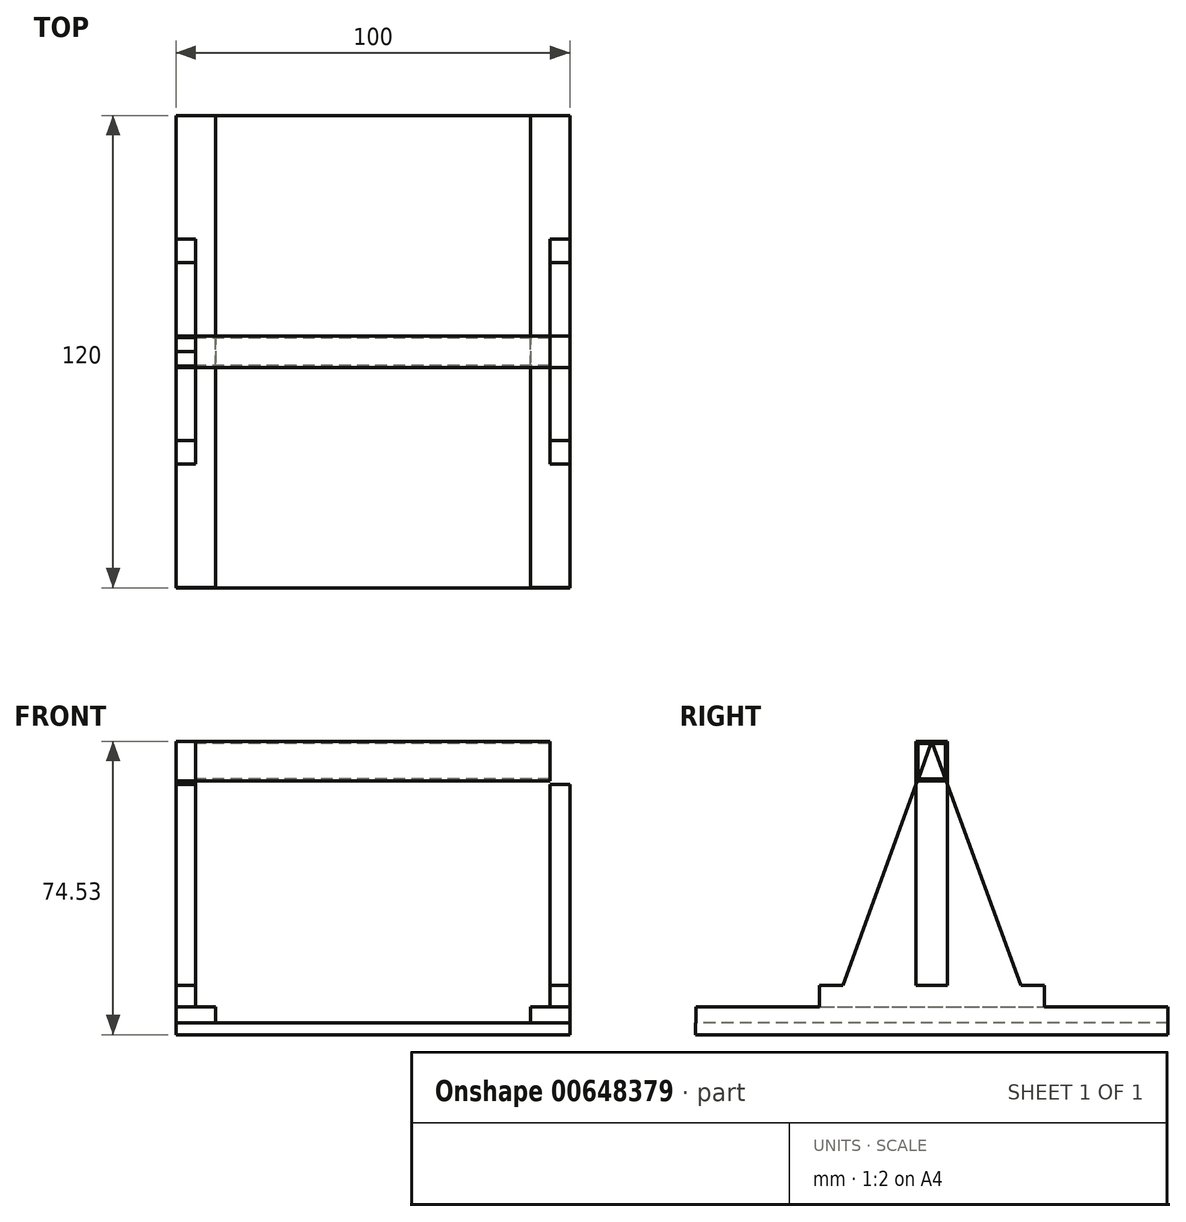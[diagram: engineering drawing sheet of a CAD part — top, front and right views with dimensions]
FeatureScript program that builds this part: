
annotation { "Feature Type Name" : "Feature", "Feature Type Description" : "" }
export const myFeature = defineFeature(function(context is Context, id is Id, definition is map)
    precondition{}
    {
        {
            var Q0;
            Q0=qCreatedBy(makeId("Right.planeOp"),FACE);
            cPlane(context, id + "F0", {"entities" : qUnion([Q0]), "cplaneType" : CPlaneType.OFFSET, "offset" : 50 * mm, "oppositeDirection" : true, "width" : 150 * mm, "height" : 150 * mm});
        }
        {
            var Q0;
            Q0=qCreatedBy(id+"F0.planeOp",FACE);
            var sketch = newSketch(context, id + "F1", { "sketchPlane" : qUnion([Q0])});
            skLineSegment(sketch, "E0", {"start": v(0, 0) * mm, "end": v(0, 62.03) * mm});
            skLineSegment(sketch, "E1", {"start": v(0, 0) * mm, "end": v(-22.58, 0) * mm});
            skLineSegment(sketch, "E2", {"start": v(-22.58, 0) * mm, "end": v(0, 62.03) * mm});
            skLineSegment(sketch, "E3.MirrorCS", {"start": v(22.58, 0) * mm, "end": v(0, 62.03) * mm});
            skLineSegment(sketch, "E4.MirrorCS", {"start": v(0, 0) * mm, "end": v(22.58, 0) * mm});
            skLineSegment(sketch, "E5.bottom", {"start": v(-28.58, 0) * mm, "end": v(28.58, 0) * mm});
            skLineSegment(sketch, "E5.top", {"start": v(-28.58, -5.5) * mm, "end": v(28.58, -5.5) * mm});
            skLineSegment(sketch, "E5.left", {"start": v(-28.58, 0) * mm, "end": v(-28.58, -5.5) * mm});
            skLineSegment(sketch, "E5.right", {"start": v(28.58, 0) * mm, "end": v(28.58, -5.5) * mm});
            skLineSegment(sketch, "E6.bottom", {"start": v(4, 0) * mm, "end": v(-4, 0) * mm});
            skLineSegment(sketch, "E6.top", {"start": v(4, 62.03) * mm, "end": v(-4, 62.03) * mm});
            skLineSegment(sketch, "E6.left", {"start": v(4, 0) * mm, "end": v(4, 62.03) * mm});
            skLineSegment(sketch, "E6.right", {"start": v(-4, 0) * mm, "end": v(-4, 62.03) * mm});
            skLineSegment(sketch, "E7.bottom", {"start": v(60, -0.5) * mm, "end": v(-59.95, -0.5) * mm});
            skLineSegment(sketch, "E7.top", {"start": v(60, -9.5) * mm, "end": v(-59.95, -9.5) * mm});
            skLineSegment(sketch, "E7.left", {"start": v(60, -0.5) * mm, "end": v(60, -9.5) * mm});
            skLineSegment(sketch, "E7.right", {"start": v(-59.95, -0.5) * mm, "end": v(-59.95, -9.5) * mm});
            skPoint(sketch, "E8", {"position": v(0, 62.03) * mm});
            skLineSegment(sketch, "E9.top", {"start": v(4, 52.03) * mm, "end": v(-4, 52.03) * mm});
            skLineSegment(sketch, "E9.left", {"start": v(4, 62.03) * mm, "end": v(4, 52.03) * mm});
            skLineSegment(sketch, "E9.right", {"start": v(-4, 62.03) * mm, "end": v(-4, 52.03) * mm});
            skLineSegment(sketch, "E10.bottom", {"start": v(60, -9.5) * mm, "end": v(-60, -9.5) * mm});
            skLineSegment(sketch, "E10.top", {"start": v(60, -12.5) * mm, "end": v(-60, -12.5) * mm});
            skLineSegment(sketch, "E10.left", {"start": v(60, -9.5) * mm, "end": v(60, -12.5) * mm});
            skLineSegment(sketch, "E10.right", {"start": v(-60, -9.5) * mm, "end": v(-60, -12.5) * mm});
            skLineSegment(sketch, "E11", {"start": v(28.58, -5.5) * mm, "end": v(60, -5.5) * mm});
            skLineSegment(sketch, "E12", {"start": v(-28.58, -5.5) * mm, "end": v(-59.95, -5.5) * mm});
            skSolve(sketch);
        }
        {
            var Q0;
            {var subQ0=sQuery(id+"F1.wireOp",EDGE,"E5.bottom");var subQ1=sQuery(id+"F1.wireOp",EDGE,"E3.MirrorCS");var subQ2=makeQuery(id+"F1.imprint","INTERSECT",VERTEX,{"derivedFrom":[subQ1,subQ0]});Q0=makeQuery(id+"F1.imprint","IMPRINT",FACE,{"disambiguationData":[TD([[makeQuery(id+"F1.imprint","IMPRINT",EDGE,{"disambiguationData":[TD([[subQ2,-1.0]])],"derivedFrom":subQ1}),1.0]])]});}
            var Q1;
            {var subQ0=sQuery(id+"F1.wireOp",EDGE,"E5.bottom");var subQ1=sQuery(id+"F1.wireOp",EDGE,"E2");var subQ2=makeQuery(id+"F1.imprint","INTERSECT",VERTEX,{"derivedFrom":[subQ1,subQ0]});Q1=makeQuery(id+"F1.imprint","IMPRINT",FACE,{"disambiguationData":[TD([[makeQuery(id+"F1.imprint","IMPRINT",EDGE,{"disambiguationData":[TD([[subQ2,-1.0]])],"derivedFrom":subQ1}),-1.0]])]});}
            var Q2;
            {var subQ1=sQuery(id+"F1.wireOp",EDGE,"E6.bottom");var subQ5=sQuery(id+"F1.wireOp",EDGE,"E0");var subQ6=makeQuery(id+"F1.imprint","INTERSECT",VERTEX,{"derivedFrom":[subQ5,subQ1]});Q2=makeQuery(id+"F1.imprint","IMPRINT",FACE,{"disambiguationData":[TD([[makeQuery(id+"F1.imprint","IMPRINT",EDGE,{"disambiguationData":[TD([[subQ6,-1.0]])],"derivedFrom":subQ5}),1.0]])]});}
            var Q3;
            {var subQ1=sQuery(id+"F1.wireOp",EDGE,"E6.bottom");var subQ5=sQuery(id+"F1.wireOp",EDGE,"E0");var subQ6=makeQuery(id+"F1.imprint","INTERSECT",VERTEX,{"derivedFrom":[subQ5,subQ1]});Q3=makeQuery(id+"F1.imprint","IMPRINT",FACE,{"disambiguationData":[TD([[makeQuery(id+"F1.imprint","IMPRINT",EDGE,{"disambiguationData":[TD([[subQ6,-1.0]])],"derivedFrom":subQ5}),-1.0]])]});}
            var Q4;
            {var subQ5=sQuery(id+"F1.wireOp",EDGE,"E9.right");Q4=makeQuery(id+"F1.imprint","IMPRINT",FACE,{"disambiguationData":[TD([[makeQuery(id+"F1.imprint","IMPRINT",EDGE,{"derivedFrom":subQ5}),1.0]])]});}
            var Q5;
            {var subQ1=sQuery(id+"F1.wireOp",EDGE,"E0");var subQ3=sQuery(id+"F1.wireOp",EDGE,"E9.top");var subQ4=makeQuery(id+"F1.imprint","INTERSECT",VERTEX,{"derivedFrom":[subQ1,subQ3]});Q5=makeQuery(id+"F1.imprint","IMPRINT",FACE,{"disambiguationData":[TD([[makeQuery(id+"F1.imprint","IMPRINT",EDGE,{"disambiguationData":[TD([[subQ4,-1.0]])],"derivedFrom":subQ3}),-1.0]])]});}
            var Q6;
            {var subQ5=sQuery(id+"F1.wireOp",EDGE,"E9.left");Q6=makeQuery(id+"F1.imprint","IMPRINT",FACE,{"disambiguationData":[TD([[makeQuery(id+"F1.imprint","IMPRINT",EDGE,{"derivedFrom":subQ5}),-1.0]])]});}
            var Q7;
            {var subQ1=sQuery(id+"F1.wireOp",EDGE,"E0");var subQ3=sQuery(id+"F1.wireOp",EDGE,"E9.top");var subQ4=makeQuery(id+"F1.imprint","INTERSECT",VERTEX,{"derivedFrom":[subQ1,subQ3]});Q7=makeQuery(id+"F1.imprint","IMPRINT",FACE,{"disambiguationData":[TD([[makeQuery(id+"F1.imprint","IMPRINT",EDGE,{"disambiguationData":[TD([[subQ4,1.0]])],"derivedFrom":subQ3}),-1.0]])]});}
            var Q8;
            {var subQ0=sQuery(id+"F1.wireOp",EDGE,"E6.right");var subQ1=sQuery(id+"F1.wireOp",EDGE,"E2");var subQ2=makeQuery(id+"F1.imprint","INTERSECT",VERTEX,{"derivedFrom":[subQ1,subQ0]});Q8=makeQuery(id+"F1.imprint","IMPRINT",FACE,{"disambiguationData":[TD([[makeQuery(id+"F1.imprint","IMPRINT",EDGE,{"disambiguationData":[TD([[subQ2,-1.0]])],"derivedFrom":subQ1}),1.0]])]});}
            var Q9;
            {var subQ0=sQuery(id+"F1.wireOp",EDGE,"E6.left");var subQ1=sQuery(id+"F1.wireOp",EDGE,"E3.MirrorCS");var subQ2=makeQuery(id+"F1.imprint","INTERSECT",VERTEX,{"derivedFrom":[subQ1,subQ0]});Q9=makeQuery(id+"F1.imprint","IMPRINT",FACE,{"disambiguationData":[TD([[makeQuery(id+"F1.imprint","IMPRINT",EDGE,{"disambiguationData":[TD([[subQ2,-1.0]])],"derivedFrom":subQ1}),-1.0]])]});}
            var Q10;
            {var subQ0=sQuery(id+"F1.wireOp",EDGE,"E5.top");Q10=makeQuery(id+"F1.imprint","IMPRINT",FACE,{"disambiguationData":[TD([[makeQuery(id+"F1.imprint","IMPRINT",EDGE,{"derivedFrom":subQ0}),1.0]])]});}
            var Q11;
            {var subQ0=sQuery(id+"F1.wireOp",EDGE,"E5.bottom");var subQ6=makeQuery(id+"F1.imprint","INTERSECT",VERTEX,{"derivedFrom":[sQuery(id+"F1.wireOp",EDGE,"E2"),subQ0]});Q11=makeQuery(id+"F1.imprint","IMPRINT",FACE,{"disambiguationData":[TD([[makeQuery(id+"F1.imprint","IMPRINT",EDGE,{"disambiguationData":[TD([[subQ6,1.0]])],"derivedFrom":subQ0}),-1.0]])]});}
            extrude(context, id + "F2", {"entities" : qUnion([Q0, Q1, Q2, Q3, Q4, Q5, Q6, Q7, Q8, Q9, Q10, Q11]), "depth" : 5 * mm, "offsetDistance" : 25 * mm});
        }
        {
            var Q0;
            {var subQ4=sQuery(id+"F1.wireOp",EDGE,"E5.top");Q0=makeQuery(id+"F1.imprint","IMPRINT",FACE,{"disambiguationData":[TD([[makeQuery(id+"F1.imprint","IMPRINT",EDGE,{"derivedFrom":subQ4}),-1.0]])]});}
            extrude(context, id + "F3", {"entities" : qUnion([Q0]), "depth" : 10 * mm, "offsetDistance" : 25 * mm});
        }
        {
            var Q0;
            Q0=makeQuery(id+"F1.imprint","IMPRINT",FACE,{"disambiguationData":[TD([[makeQuery(id+"F1.imprint","IMPRINT",EDGE,{"derivedFrom":sQuery(id+"F1.wireOp",EDGE,"E10.top")}),-1.0]])]});
            extrude(context, id + "F4", {"entities" : qUnion([Q0]), "operationType" : NewBodyOperationType.ADD, "depth" : 50 * mm, "offsetDistance" : 25 * mm});
        }
        {
            var Q0;
            Q0=qCreatedBy(id+"F0.planeOp",FACE);
            cPlane(context, id + "F5", {"entities" : qUnion([Q0]), "cplaneType" : CPlaneType.OFFSET, "offset" : 5 * mm, "width" : 150 * mm, "height" : 150 * mm});
        }
        {
            var Q0;
            Q0=qCreatedBy(id+"F5.planeOp",FACE);
            var sketch = newSketch(context, id + "F6", { "sketchPlane" : qUnion([Q0])});
            skLineSegment(sketch, "E13.0", {"start": v(4, 52.03) * mm, "end": v(-4, 52.03) * mm});
            skLineSegment(sketch, "E14.0", {"start": v(4, 62.03) * mm, "end": v(-4, 62.03) * mm});
            skLineSegment(sketch, "E15", {"start": v(-4, 62.03) * mm, "end": v(-4, 52.03) * mm});
            skLineSegment(sketch, "E16", {"start": v(4, 62.03) * mm, "end": v(4, 52.03) * mm});
            skLineSegment(sketch, "E17.bottom", {"start": v(-3.5, 61.53) * mm, "end": v(3.5, 61.53) * mm});
            skLineSegment(sketch, "E17.top", {"start": v(-3.5, 52.53) * mm, "end": v(3.5, 52.53) * mm});
            skLineSegment(sketch, "E17.left", {"start": v(-3.5, 61.53) * mm, "end": v(-3.5, 52.53) * mm});
            skLineSegment(sketch, "E17.right", {"start": v(3.5, 61.53) * mm, "end": v(3.5, 52.53) * mm});
            skLineSegment(sketch, "E18", {"start": v(-3.5, 61.53) * mm, "end": v(-4, 62.03) * mm});
            skLineSegment(sketch, "E19", {"start": v(3.5, 61.53) * mm, "end": v(4, 62.03) * mm});
            skLineSegment(sketch, "E20", {"start": v(3.5, 52.53) * mm, "end": v(4, 52.03) * mm});
            skLineSegment(sketch, "E21", {"start": v(-4, 52.03) * mm, "end": v(-3.5, 52.53) * mm});
            skLineSegment(sketch, "E22", {"start": v(-3.5, 57.03) * mm, "end": v(-4, 57.03) * mm});
            skLineSegment(sketch, "E23", {"start": v(0, 61.53) * mm, "end": v(0, 62.03) * mm});
            skLineSegment(sketch, "E24", {"start": v(3.5, 57.03) * mm, "end": v(4, 57.03) * mm});
            skLineSegment(sketch, "E25", {"start": v(0, 52.53) * mm, "end": v(0, 52.03) * mm});
            skSolve(sketch);
        }
        {
            var Q0;
            Q0 = qSketchRegion(id + "F6", true);
            extrude(context, id + "F7", {"entities" : qUnion([Q0]), "depth" : 45 * mm, "offsetDistance" : 25 * mm});
        }
        {
            var Q0;
            Q0=makeQuery(id+"F2.opExtrude","SWEPT_BODY",BODY,{"disambiguationData":[OSD([sQuery(id+"F1.wireOp",EDGE,"E2"),sQuery(id+"F1.wireOp",EDGE,"E3.MirrorCS"),sQuery(id+"F1.wireOp",EDGE,"E5.bottom"),sQuery(id+"F1.wireOp",EDGE,"E5.top"),sQuery(id+"F1.wireOp",EDGE,"E5.left"),sQuery(id+"F1.wireOp",EDGE,"E5.right"),sQuery(id+"F1.wireOp",EDGE,"E6.left"),sQuery(id+"F1.wireOp",EDGE,"E6.right"),sQuery(id+"F1.wireOp",EDGE,"E6.top"),sQuery(id+"F1.wireOp",EDGE,"E9.left"),sQuery(id+"F1.wireOp",EDGE,"E9.right")])]});
            var Q1;
            Q1=qCreatedBy(makeId("Right.planeOp"),FACE);
            mirror(context, id + "F8", {"entities" : qUnion([Q0]), "mirrorPlane" : qUnion([Q1])});
        }
        {
            var Q0;
            Q0=makeQuery(id+"F3.opExtrude","SWEPT_BODY",BODY,{"disambiguationData":[OSD([sQuery(id+"F1.wireOp",EDGE,"E5.top"),sQuery(id+"F1.wireOp",EDGE,"E7.left"),sQuery(id+"F1.wireOp",EDGE,"E7.right"),sQuery(id+"F1.wireOp",EDGE,"E10.bottom"),sQuery(id+"F1.wireOp",EDGE,"E11"),sQuery(id+"F1.wireOp",EDGE,"E12")])]});
            var Q1;
            Q1=qCreatedBy(makeId("Right.planeOp"),FACE);
            mirror(context, id + "F9", {"operationType" : NewBodyOperationType.ADD, "entities" : qUnion([Q0]), "mirrorPlane" : qUnion([Q1])});
        }
        {
            var Q0;
            Q0=makeQuery(id+"F7.opExtrude","SWEPT_BODY",BODY,{"disambiguationData":[OSD([sQuery(id+"F6.wireOp",EDGE,"E13.0"),sQuery(id+"F6.wireOp",EDGE,"E14.0"),sQuery(id+"F6.wireOp",EDGE,"E15"),sQuery(id+"F6.wireOp",EDGE,"E16")])]});
            var Q1;
            Q1=qCreatedBy(makeId("Right.planeOp"),FACE);
            mirror(context, id + "F10", {"operationType" : NewBodyOperationType.ADD, "entities" : qUnion([Q0]), "mirrorPlane" : qUnion([Q1])});
        }
    });
